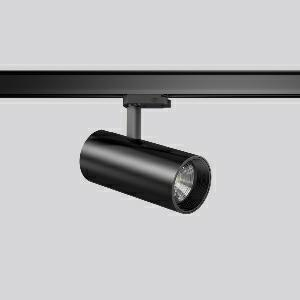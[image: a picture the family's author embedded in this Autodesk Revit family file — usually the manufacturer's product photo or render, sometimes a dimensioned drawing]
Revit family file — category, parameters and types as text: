
# Revit family: deecos_s_mini_742194_003_e664
name_source: partatom
category: Lighting Fixtures
units: mm (PartAtom-declared; Revit-internal decimal feet)

## family parameters
Cut with Voids When Loaded = No
Host = Face
Light Source = No
Part Type = Normal
Room Calculation Point = No
Round Connector Dimension = Use Diameter
Shared = No

## types (1)
- DEECOS S mini (1 x LED Modul 930, 2000 lm, 3000)
    Apparent Load = 22 VA
    Approval mark = CE
    CIE Flux Codes = 99 100 100 100 100
    Color Rendering = 90
    Color Temperature = 3000
    Default Elevation = 1800 mm
    Description = Series: DEECOS S mini
LED surface-mounted projector in modern design with no visible cooling ribs. Housing: die-cast aluminium, powder-coated. Rotation range: 356°. Swivel range: 90°. Black plastic ring and recessed LED to prevent glare from the side. Optical assembly with lens made of plastic (polycarbonate) for the best homogeneous light distribution - can be changed without tools. Best colour rendering index Ra>90. Superspot version with small spot LED. With multi adaptor for 3-circuit tracks 230 V. Suitable for Track on ceiling, Wall track. High quality converter without flickering and stroboscopic effect. The following accessories can be mounted without use of tools: interchangeable lenses, decorative glasses, honeycomb louvre, clear and frosted diffusers, white interchangeable plastic ring. 
Colour: deep black, matt (RAL 9005)
Diameter: 87 mm
Height: 214 mm
Lamp: LED
Socket: without socket
Colour temperature: 3000K
Colour rendering index (CRI): 92
System power: 22 W
Rated luminous flux: 2000 lm
Luminous efficiency: 91 lm/W
Control gear: Regulated power supply
Protection class: I
Type of protection: IP 20
    Height = 214 mm
    Lamp = 1 x LED Modul 930
    Lamp Light Flux = 2000 lm
    Lamp count = 1
    Length = 87 mm
    Lifetime = 50000 h
    Luminous efficacy = 91 lm/W
    Manufacturer = RZB
    ModVariant = No
    Model = 742194.003
    Mounting Place = Ceiling
    Mounting Type = Rail mounted
    Number of Poles = 1
    OnlyDefault = Yes
    Power Factor = 1
    Product Name = DEECOS S mini
    Product group = Track mounted projectors
    ProductGroupID = 301
    Protection Class = Protection class I
    Protection Degree = IP 20
    RLX_Detail_Level = 1
    RLX_Emergency_Light_Flux = 0 lm
    RLX_Emergency_Type = 0
    RLX_Emergency_Type_DB = No
    RlxData = <blob elided: 38593 chars, md5=9bc42c8e>
    Socket = socket
    Standby Power = 0 W
    System Light Flux = 2000 lm
    System Power = 22 W
    Type Comments = Product without accessories
    Type Image = 741930.003.jpg
    URL = http://relux.com
    VarID = ---
    Voltage = 230 V
    Voltage Range = 220-240 V
    Weight = 0.00 kg
    Width = 0 mm  [stored 0 ft]

note: [stored X ft] marks values corroborated as IEEE doubles in the binary element streams (Revit-internal decimal feet)

## geometry (parser evidence)
native form markers: Blend x4, Sweep x13
no freeform markers — native parametric forms only
